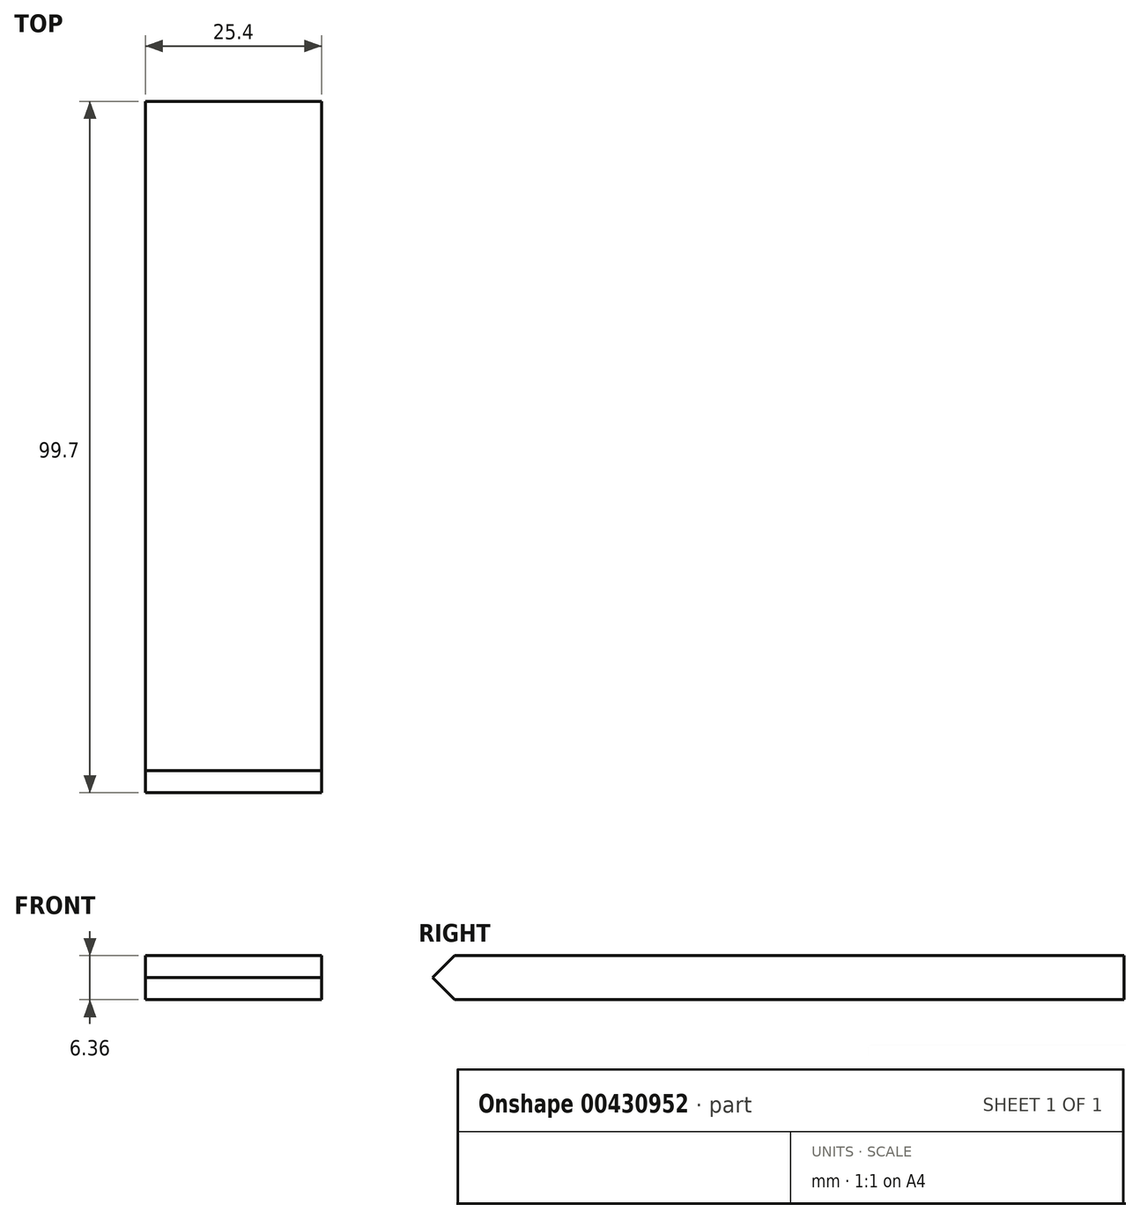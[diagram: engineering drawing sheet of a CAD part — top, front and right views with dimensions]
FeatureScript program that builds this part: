
annotation { "Feature Type Name" : "Feature", "Feature Type Description" : "" }
export const myFeature = defineFeature(function(context is Context, id is Id, definition is map)
    precondition{}
    {
        {
            var Q0;
            Q0=qCreatedBy(makeId("Front.planeOp"),FACE);
            var sketch = newSketch(context, id + "F0", { "sketchPlane" : qUnion([Q0])});
            skLineSegment(sketch, "E0.bottom", {"start": v(12.7, -3.17) * mm, "end": v(-12.7, -3.18) * mm});
            skLineSegment(sketch, "E0.top", {"start": v(12.7, 3.18) * mm, "end": v(-12.7, 3.18) * mm});
            skLineSegment(sketch, "E0.left", {"start": v(12.7, -3.17) * mm, "end": v(12.7, 3.18) * mm});
            skLineSegment(sketch, "E0.right", {"start": v(-12.7, -3.18) * mm, "end": v(-12.7, 3.17) * mm});
            skPoint(sketch, "E0.middle", {"position": v(0, 0) * mm});
            skSolve(sketch);
        }
        {
            var Q0;
            Q0 = qSketchRegion(id + "F0", true);
            extrude(context, id + "F1", {"entities" : qUnion([Q0]), "depth" : 101.6 * mm});
        }
        {
            var Q0;
            Q0=makeQuery(id+"F1.opExtrude","CAP_EDGE",EDGE,{"disambiguationData":[OSD([sQuery(id+"F0.wireOp",EDGE,"E0.top")])],"isStart":false});
            var Q1;
            Q1=makeQuery(id+"F1.opExtrude","CAP_EDGE",EDGE,{"disambiguationData":[OSD([sQuery(id+"F0.wireOp",EDGE,"E0.bottom")])],"isStart":false});
            chamfer(context, id + "F2", {"entities" : qUnion([Q0, Q1]), "width" : 5.08 * mm, "tangentPropagation" : true});
        }
    });
